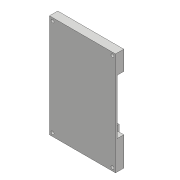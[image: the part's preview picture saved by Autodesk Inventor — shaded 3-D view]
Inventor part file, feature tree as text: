
AUTODESK INVENTOR PART (.ipt)
format: ipt  version: 2018 (Build 220112000, 112)  size: 310,784 bytes
history: native  units: mm
features: sketch x7, extrude x6, hole x1
ambient origin geometry x8: Origin, YZ Plane, XZ Plane, XY Plane, X Axis, Y Axis, Z Axis, Center Point
bodies: Solid1 (feature_tree)
feature tree (14):
  extrude  "Extrusion1"  Depth=68.59mm
  extrude  "Extrusion2"  Depth=20.0mm
  extrude  "Extrusion3"  Depth=7.0mm TaperAngle=0.0deg
  extrude  "Extrusion4"  Depth=16.0mm
  hole  "Hole1"  [1 undecoded]
  extrude  "Extrusion5"  Depth=7.0mm TaperAngle=0.0deg
  extrude  "Extrusion6"  Depth=3.18mm
  sketch  "Sketch1"  dims[d0=106.92mm d1=68.59mm]
  sketch  "Sketch2"  dims[d2=1.6mm d3=0.0mm d4=20.0mm]
  sketch  "Sketch3"  dims[d5=30.0mm d6=7.0mm d7=0.0mm]
  sketch  "Sketch4"  dims[d8=19.93mm d9=16.0mm]
  sketch  "Sketch5"  dims[d10=7.0mm d11=0.0mm d12=12.0mm]
  sketch  "Sketch6"  dims[d13=10.0mm d14=7.0mm d15=0.0mm]
  sketch  "Sketch7"  dims[d16=3.18mm d17=3.18mm d18=3.18mm d19=3.3mm d20=3.2mm d21=6.0mm d22=6.3mm d23=2.0mm d24=90.0deg d25=8.0mm d26=20.594885mm d27=24.0mm d28=24.0mm d29=6.0mm d30=3.0mm d31=0.0mm d32=1.0mm d33=0.0mm]
note: 1 required parameter value undecoded (feature->parameter linkage not recoverable at this tier; creation-order binding heuristic only, values carry confidence <= 0.55)
